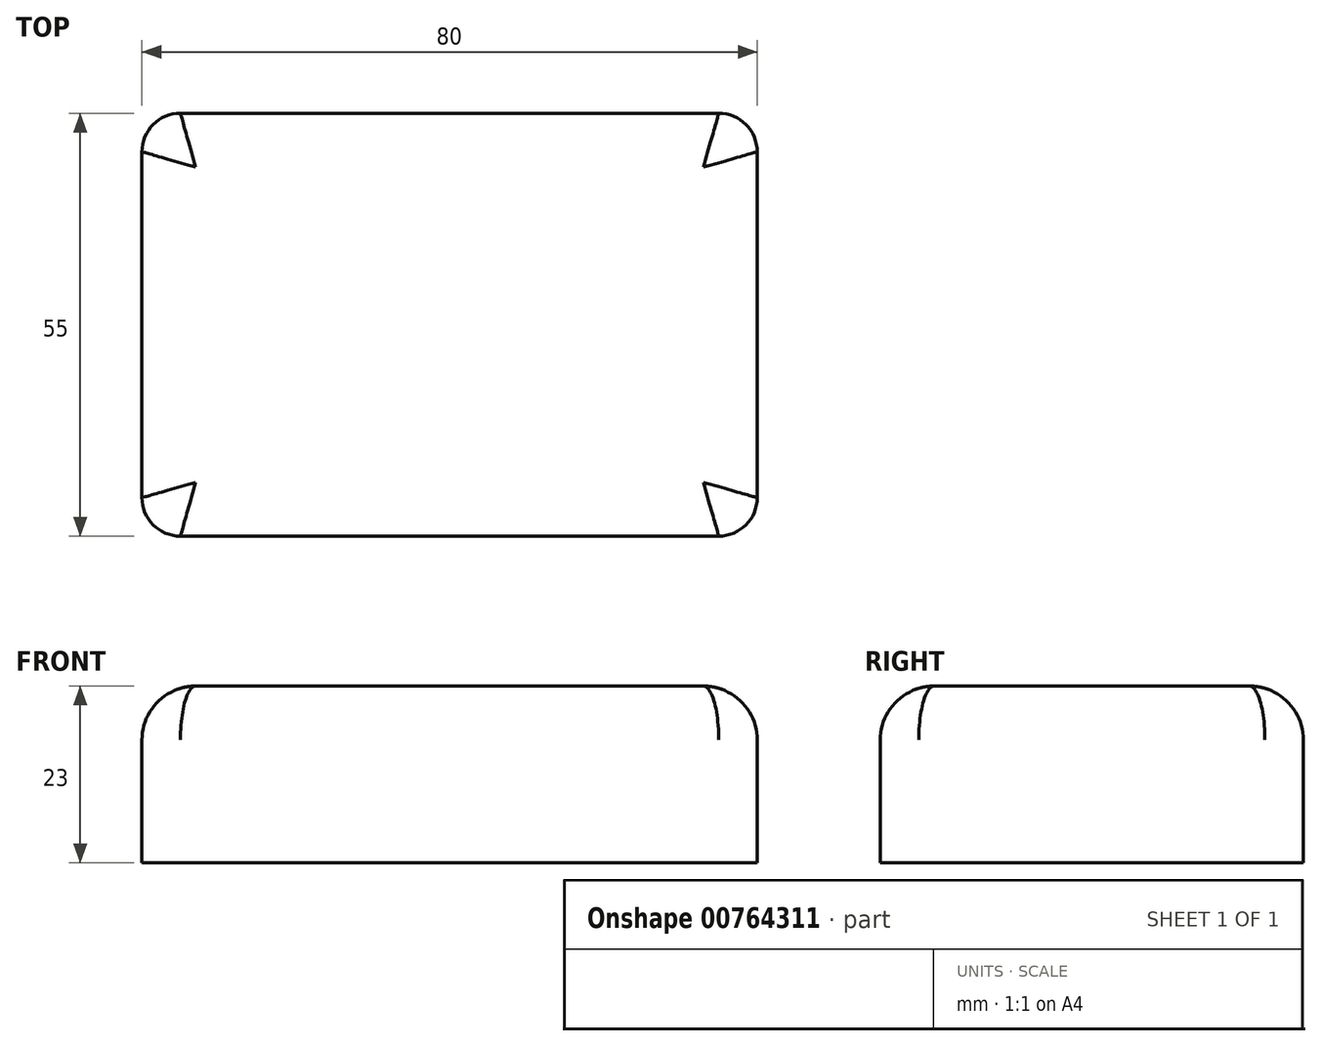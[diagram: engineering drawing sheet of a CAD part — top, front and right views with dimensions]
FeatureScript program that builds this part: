
annotation { "Feature Type Name" : "Feature", "Feature Type Description" : "" }
export const myFeature = defineFeature(function(context is Context, id is Id, definition is map)
    precondition{}
    {
        {
            var Q0;
            Q0=qCreatedBy(makeId("Top.planeOp"),FACE);
            var sketch = newSketch(context, id + "F0", { "sketchPlane" : qUnion([Q0])});
            skLineSegment(sketch, "E0.bottom", {"start": v(40, 27.5) * mm, "end": v(-40, 27.5) * mm});
            skLineSegment(sketch, "E0.top", {"start": v(40, -27.5) * mm, "end": v(-40, -27.5) * mm});
            skLineSegment(sketch, "E0.left", {"start": v(40, 27.5) * mm, "end": v(40, -27.5) * mm});
            skLineSegment(sketch, "E0.right", {"start": v(-40, 27.5) * mm, "end": v(-40, -27.5) * mm});
            skPoint(sketch, "E0.middle", {"position": v(0, 0) * mm});
            skSolve(sketch);
        }
        {
            var Q0;
            Q0 = qSketchRegion(id + "F0", true);
            extrude(context, id + "F1", {"entities" : qUnion([Q0]), "depth" : 23 * mm, "offsetDistance" : 25 * mm});
        }
        {
            var Q0;
            Q0=makeQuery(id+"F1.opExtrude","SWEPT_EDGE",EDGE,{"disambiguationData":[OSD([sQuery(id+"F0.wireOp",EDGE,"E0.bottom"),sQuery(id+"F0.wireOp",EDGE,"E0.right")])]});
            var Q1;
            Q1=makeQuery(id+"F1.opExtrude","SWEPT_EDGE",EDGE,{"disambiguationData":[OSD([sQuery(id+"F0.wireOp",EDGE,"E0.top"),sQuery(id+"F0.wireOp",EDGE,"E0.right")])]});
            var Q2;
            Q2=makeQuery(id+"F1.opExtrude","SWEPT_EDGE",EDGE,{"disambiguationData":[OSD([sQuery(id+"F0.wireOp",EDGE,"E0.top"),sQuery(id+"F0.wireOp",EDGE,"E0.left")])]});
            var Q3;
            Q3=makeQuery(id+"F1.opExtrude","SWEPT_EDGE",EDGE,{"disambiguationData":[OSD([sQuery(id+"F0.wireOp",EDGE,"E0.bottom"),sQuery(id+"F0.wireOp",EDGE,"E0.left")])]});
            fillet(context, id + "F2", {"entities" : qUnion([Q0, Q1, Q2, Q3]), "radius" : 5 * mm, "tangentPropagation" : true, "allowEdgeOverflow" : false});
        }
        {
            var Q0;
            Q0=makeQuery(id+"F1.opExtrude","CAP_EDGE",EDGE,{"disambiguationData":[OSD([sQuery(id+"F0.wireOp",EDGE,"E0.right")])],"isStart":false});
            fillet(context, id + "F3", {"entities" : qUnion([Q0]), "radius" : 7 * mm, "tangentPropagation" : true, "allowEdgeOverflow" : false});
        }
    });
